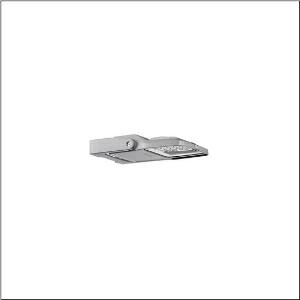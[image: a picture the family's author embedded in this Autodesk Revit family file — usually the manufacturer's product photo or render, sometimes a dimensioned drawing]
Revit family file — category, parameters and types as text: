
# Revit family: floodlight_fl_21_iq_micro___pl33t_5xa7762a4f2a_0497
name_source: partatom
category: Lighting Fixtures
units: mm (PartAtom-declared; Revit-internal decimal feet)

## family parameters
Cut with Voids When Loaded = No
Host = Face
Light Source = No
Part Type = Normal
Room Calculation Point = No
Round Connector Dimension = Use Diameter
Shared = No

## types (1)
- --- (1 x LED, 3050 lm, 23.1 W, 4000K)
    Apparent Load = 23 VA
    CIE Flux Codes = 26 75 99 100 100
    Color Rendering = 70
    Color Temperature = 4000K
    Default Elevation = 1800 mm
    Description = Floodlight FL 21 iQ micro, floodlight, primary light control with lens, of PMMA, primary optical cover: protective disc, of toughened safety glass, transparent, light distribution: PL33T, light emission: direct distribution, installation type: surface-mounted, LED, High Power LED, rated luminous flux: 3.050lm, luminous efficacy: 132lm/W, light colour: 740, colour temperature: 4000K, control: Auto-Match, Temp-Guard, Night-Set, Smart-Wire, Desk-Remote (wireless, voltage-free reading and setting of iQ features in the workshop via application-optimized NFC function/RFID function), optimised constant luminous flux control (CLO 2.0), Street-Remote, with terminal, 6-pole, mains connection: 220..240V, AC, 50/60Hz, start of lifetime: 23W, end of service life: 24W, reduction: 11W, luminaire housing, of diecast aluminium, powder-coated, Siteco® metallic grey (DB 702S), corrosivity category C5 mid according to DIN EN ISO 12944, sealing non-destructively replaceable, design bracket, of diecast aluminium, powder-coated, Siteco® metallic grey (DB 702S), protection rating (complete): IP66, insulation class (complete): insulation class II (safety insulation), certification: CE, ENEC, VDE, protection symbol: D, impact resistance: IK07, permissible operating ambient temperature: -40..+40°C, permissible operating ambient temperature for outdoor applications: -40..+50°C, standard: DIN EN 12944, LABS conformity tested according to VDMA 24364:2018-05, packaging unit: 1 piece

Light Distribution: PL33T
    Height = 65 mm
    Lamp = 1 x LED
    Lamp Light Flux = 3050 lm
    Lamp Power = 23.1 W
    Lamp count = 1
    Length = 312 mm
    Luminous efficacy = 132 lm/W
    Manufacturer = Siteco
    ModVariant = No
    Model = 5XA7762A4F2A
    Mounting Place = Wall
    Mounting Type = Surface mounted
    Number of Poles = 1
    OnlyDefault = Yes
    Power Factor = 1
    Product Name = Floodlight FL 21 iQ micro | PL33T
    Product group = floodlight | wall mounted
    ProductGroupID = 2001
    Protection Class = Protection class II
    Protection Degree = IP 66
    RLX_Detail_Level = 1
    RLX_Emergency_Light_Flux = 0 lm
    RLX_Emergency_Type = 0
    RLX_Emergency_Type_DB = No
    RlxData = <blob elided: 97349 chars, md5=8ba4e1df>
    Socket = socket
    Standby Power = 0 W
    System Light Flux = 3050 lm
    System Power = 23 W
    Type Comments = factory setting: luminous flux: 100 % | dim-lin: 254 | 455 mA
    Type Image = l_1006878.jpg
    URL = http://relux.com
    VarID = @adj_098059
    Voltage = 0 V
    Weight = 0.00 kg
    Width = 230 mm

## geometry (parser evidence)
native form markers: Blend x4, Sweep x13
no freeform markers — native parametric forms only
